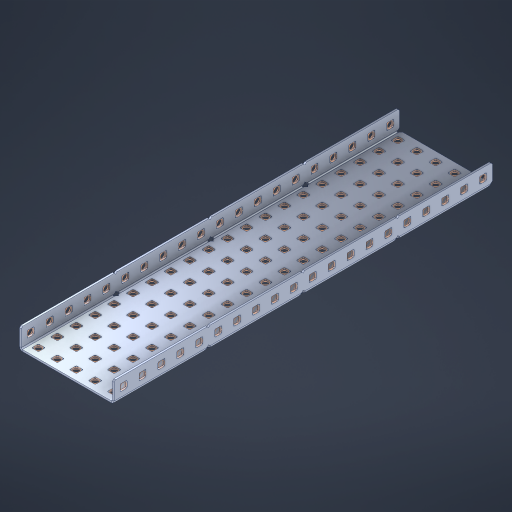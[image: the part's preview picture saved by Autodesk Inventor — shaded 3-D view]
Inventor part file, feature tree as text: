
AUTODESK INVENTOR PART (.ipt)
format: ipt  version: 2023 (Build 270158000, 158)  size: 1,673,728 bytes
history: native  units: in
note: dims shown in document units (in); Inventor stores cm internally (conversion verified against a paired STEP export)
features: other x145, extrude x139, sheet_metal_op x10, sketch x8, mirror x1, pattern_linear x1, chamfer x1
ambient origin geometry x8: Origin, YZ Plane, XZ Plane, XY Plane, X Axis, Y Axis, Z Axis, Center Point
bodies: Solid1 (feature_tree), Body (feature_tree)
feature tree (305):
  other  "Flange Pattern Plane"
  sheet_metal_op  "Flange Pattern"
  sheet_metal_op  "Body Pattern"
  other  "Arc Length"
  mirror  "Notch Mirror"
  pattern_linear  "Notch Pattern"  Spacing1=0.1875in  [1 undecoded]
  chamfer  "End Chamfer"
  extrude  "Half Cut"  Depth=0.0469in
  sketch  "Sketch1"  dims[d0=2.5in]
  other  "Plate1"
  sketch  "Sketch2"  dims[d1=10.0in]
  other  "Plate2"
  sheet_metal_op  "Bend1"
  sheet_metal_op  "Corner1"
  sketch  "Sketch3"  dims[d2=0.0469in]
  other  "Flange Pattern Sketch"
  sketch  "Sketch7"  dims[d3=0.0469in]
  other  "Srf1"
  other  "Srf2"
  sketch  "Sketch8"  dims[d4=0.0234in]
  sketch  "Sketch9"  dims[d5=0.0938in]
  other  "Srf91"
  sheet_metal_op  "Body Pattern Sketch"
  other  "Srf92"
  sketch  "Sketch13"  dims[d6=0.0469in]
  sketch  "Sketch14"  dims[d7=0.5in d8=90.0deg d9=0.0312in d10=0.1875in d11=0.0469in d12=0.0469in d16=0.182in d17=0.02in d18=0.0469in d19=0.0in d20=0.25in d21=0.25in d46=0.172in d47=1.0in d48=0.0in d49=0.182in d50=0.02in d51=0.25in d52=0.25in d53=0.0469in d54=0.0in d55=0.172in d56=1.0in d57=0.0in d60=7.874in d62=0.5in d63=1.9685in d65=0.5in d85=0.1227in d86=0.1659in d88=0.04in d89=0.0469in d90=0.0in d91=0.04in d92=0.0491in d95=2.5in d96=0.04in d97=0.25in d98=45.0deg d101=0.0in d102=2.497in d131=2.5in d132=7.874in d134=0.5in d139=0.5in]
  other  "Srf856"
  other  "Srf1310"
  other  "Srf1311"
  other  "Srf1312"
  other  "Srf1376"
  other  "Srf1377"
  other  "Srf1728"
  other  "Srf1755"
  other  "Srf1878"
  other  "Srf1879"
  other  "Srf1880"
  other  "Srf1881"
  other  "Srf1882"
  other  "Srf1883"
  other  "Srf1884"
  other  "Srf1885"
  other  "Srf1886"
  other  "Srf1887"
  other  "Srf1888"
  other  "Srf1889"
  other  "Srf1890"
  other  "Srf1891"
  other  "Srf1892"
  other  "Srf1893"
  other  "Srf1894"
  other  "Srf1895"
  other  "Srf1896"
  other  "Srf1897"
  other  "Srf1898"
  other  "Srf1899"
  other  "Srf1900"
  other  "Srf1901"
  other  "Srf1902"
  other  "Srf1903"
  other  "Srf1904"
  other  "Srf1905"
  other  "Srf1906"
  other  "Srf1942"
  other  "Srf1943"
  other  "Srf1944"
  other  "Srf1945"
  other  "Srf1946"
  other  "Srf1947"
  other  "Srf1948"
  other  "Srf1949"
  other  "Srf1950"
  other  "Srf1951"
  other  "Srf1952"
  other  "Srf1953"
  other  "Srf1954"
  other  "Srf1955"
  other  "Srf1956"
  other  "Srf1957"
  other  "Srf1958"
  other  "Srf1959"
  other  "Srf1960"
  other  "Srf1961"
  other  "Srf1962"
  other  "Srf1963"
  other  "Srf1964"
  other  "Srf1965"
  other  "Srf1966"
  other  "Srf1967"
  other  "Srf1968"
  other  "Srf1969"
  other  "Srf1970"
  other  "Srf2111"
  other  "Srf2112"
  other  "Srf2113"
  other  "Srf2114"
  other  "Srf2115"
  other  "Srf2146"
  other  "Srf2147"
  other  "Srf2148"
  other  "Srf2149"
  other  "Srf2150"
  other  "Srf2151"
  other  "Srf2152"
  other  "Srf2153"
  other  "Srf2154"
  other  "Srf2155"
  other  "Srf2156"
  other  "Srf2157"
  other  "Srf2158"
  other  "Srf2159"
  other  "Srf2160"
  other  "Srf2161"
  other  "Srf2162"
  other  "Srf2163"
  other  "Srf2164"
  other  "Srf2165"
  other  "Srf2166"
  other  "Srf2167"
  other  "Srf2168"
  other  "Srf2169"
  other  "Srf2170"
  other  "Srf2171"
  other  "Srf2172"
  other  "Srf2173"
  other  "Srf2174"
  other  "Srf2175"
  other  "Srf2176"
  other  "Srf2177"
  other  "Srf2178"
  other  "Srf2179"
  other  "Srf2180"
  other  "Srf2181"
  other  "Srf2182"
  other  "Srf2183"
  other  "Srf2184"
  other  "Srf2185"
  other  "Srf2186"
  other  "Srf2187"
  other  "Srf2188"
  other  "Srf2189"
  other  "Srf2190"
  other  "Srf2191"
  other  "Srf2192"
  other  "Srf2193"
  other  "Srf2194"
  other  "Srf2195"
  other  "Srf2196"
  other  "Srf2197"
  other  "Srf2198"
  other  "Srf2199"
  other  "Srf2200"
  other  "Srf2201"
  other  "Srf2202"
  other  "Srf2203"
  other  "Srf2204"
  other  "Srf2205"
  other  "Srf2206"
  other  "Srf2207"
  other  "Srf2208"
  other  "Srf2209"
  other  "Srf2210"
  sheet_metal_op  "Flange Stamp"
  sheet_metal_op  "Flange Circle"
  sheet_metal_op  "Body Stamp"
  sheet_metal_op  "Body Circle"
  sheet_metal_op  "Notch"
  extrude  "ExtrusionSrf2"  Depth=0.0469in
  extrude  "ExtrusionSrf92"  Depth=2.5in
  extrude  "ExtrusionSrf856"  Depth=0.02in
  extrude  "ExtrusionSrf1310"  Depth=0.0469in
  extrude  "ExtrusionSrf1311"  TaperAngle=0.0deg  [1 undecoded]
  extrude  "ExtrusionSrf1312"  Depth=0.25in
  extrude  "ExtrusionSrf1376"  Depth=0.25in
  extrude  "ExtrusionSrf1377"  Depth=2.5in
  extrude  "ExtrusionSrf1728"  Depth=2.5in TaperAngle=0.0deg
  extrude  "ExtrusionSrf1755"  Depth=2.5in
  extrude  "ExtrusionSrf1878"  Depth=0.02in
  extrude  "ExtrusionSrf1879"  Depth=0.25in
  extrude  "ExtrusionSrf1880"  Depth=0.25in
  extrude  "ExtrusionSrf1881"  Depth=0.0469in
  extrude  "ExtrusionSrf1882"  TaperAngle=0.0deg  [1 undecoded]
  extrude  "ExtrusionSrf1883"  Depth=2.5in
  extrude  "ExtrusionSrf1884"  Depth=2.5in TaperAngle=0.0deg
  extrude  "ExtrusionSrf1885"  Depth=2.5in
  extrude  "ExtrusionSrf1886"  Depth=2.5in
  extrude  "ExtrusionSrf1887"  Depth=2.5in
  extrude  "ExtrusionSrf1888"  Depth=2.5in
  extrude  "ExtrusionSrf1889"  Depth=2.5in
  extrude  "ExtrusionSrf1890"  Depth=0.0469in
  extrude  "ExtrusionSrf1891"  TaperAngle=0.0deg  [1 undecoded]
  extrude  "ExtrusionSrf1892"  Depth=2.5in
  extrude  "ExtrusionSrf1893"  Depth=2.5in
  extrude  "ExtrusionSrf1894"  Depth=2.5in
  extrude  "ExtrusionSrf1895"  Depth=0.25in TaperAngle=45.0deg
  extrude  "ExtrusionSrf1896"  TaperAngle=0.0deg  [1 undecoded]
  extrude  "ExtrusionSrf1897"  Depth=2.5in
  extrude  "ExtrusionSrf1898"  Depth=2.5in
  extrude  "ExtrusionSrf1899"  Depth=2.5in
  extrude  "ExtrusionSrf1900"  Depth=2.5in
  extrude  "ExtrusionSrf1901"  Depth=2.5in
  extrude  "ExtrusionSrf1902"  [1 undecoded]
  extrude  "ExtrusionSrf1903"  [1 undecoded]
  extrude  "ExtrusionSrf1904"  [1 undecoded]
  extrude  "ExtrusionSrf1905"  [1 undecoded]
  extrude  "ExtrusionSrf1906"  [1 undecoded]
  extrude  "ExtrusionSrf1942"  [1 undecoded]
  extrude  "ExtrusionSrf1943"  [1 undecoded]
  extrude  "ExtrusionSrf1944"  [1 undecoded]
  extrude  "ExtrusionSrf1945"  [1 undecoded]
  extrude  "ExtrusionSrf1946"  [1 undecoded]
  extrude  "ExtrusionSrf1947"  [1 undecoded]
  extrude  "ExtrusionSrf1948"  [1 undecoded]
  extrude  "ExtrusionSrf1949"  [1 undecoded]
  extrude  "ExtrusionSrf1950"  [1 undecoded]
  extrude  "ExtrusionSrf1951"  [1 undecoded]
  extrude  "ExtrusionSrf1952"  [1 undecoded]
  extrude  "ExtrusionSrf1953"  [1 undecoded]
  extrude  "ExtrusionSrf1954"  [1 undecoded]
  extrude  "ExtrusionSrf1955"  [1 undecoded]
  extrude  "ExtrusionSrf1956"  [1 undecoded]
  extrude  "ExtrusionSrf1957"  [1 undecoded]
  extrude  "ExtrusionSrf1958"  [1 undecoded]
  extrude  "ExtrusionSrf1959"  [1 undecoded]
  extrude  "ExtrusionSrf1960"  [1 undecoded]
  extrude  "ExtrusionSrf1961"  [1 undecoded]
  extrude  "ExtrusionSrf1962"  [1 undecoded]
  extrude  "ExtrusionSrf1963"  [1 undecoded]
  extrude  "ExtrusionSrf1964"  [1 undecoded]
  extrude  "ExtrusionSrf1965"  [1 undecoded]
  extrude  "ExtrusionSrf1966"  [1 undecoded]
  extrude  "ExtrusionSrf1967"  [1 undecoded]
  extrude  "ExtrusionSrf1968"  [1 undecoded]
  extrude  "ExtrusionSrf1969"  [1 undecoded]
  extrude  "ExtrusionSrf1970"  [1 undecoded]
  extrude  "ExtrusionSrf2111"  [1 undecoded]
  extrude  "ExtrusionSrf2112"  [1 undecoded]
  extrude  "ExtrusionSrf2113"  [1 undecoded]
  extrude  "ExtrusionSrf2114"  [1 undecoded]
  extrude  "ExtrusionSrf2115"  [1 undecoded]
  extrude  "ExtrusionSrf2146"  [1 undecoded]
  extrude  "ExtrusionSrf2147"  [1 undecoded]
  extrude  "ExtrusionSrf2148"  [1 undecoded]
  extrude  "ExtrusionSrf2149"  [1 undecoded]
  extrude  "ExtrusionSrf2150"  [1 undecoded]
  extrude  "ExtrusionSrf2151"  [1 undecoded]
  extrude  "ExtrusionSrf2152"  [1 undecoded]
  extrude  "ExtrusionSrf2153"  [1 undecoded]
  extrude  "ExtrusionSrf2154"  [1 undecoded]
  extrude  "ExtrusionSrf2155"  [1 undecoded]
  extrude  "ExtrusionSrf2156"  [1 undecoded]
  extrude  "ExtrusionSrf2157"  [1 undecoded]
  extrude  "ExtrusionSrf2158"  [1 undecoded]
  extrude  "ExtrusionSrf2159"  [1 undecoded]
  extrude  "ExtrusionSrf2160"  [1 undecoded]
  extrude  "ExtrusionSrf2161"  [1 undecoded]
  extrude  "ExtrusionSrf2162"  [1 undecoded]
  extrude  "ExtrusionSrf2163"  [1 undecoded]
  extrude  "ExtrusionSrf2164"  [1 undecoded]
  extrude  "ExtrusionSrf2165"  [1 undecoded]
  extrude  "ExtrusionSrf2166"  [1 undecoded]
  extrude  "ExtrusionSrf2167"  [1 undecoded]
  extrude  "ExtrusionSrf2168"  [1 undecoded]
  extrude  "ExtrusionSrf2169"  [1 undecoded]
  extrude  "ExtrusionSrf2170"  [1 undecoded]
  extrude  "ExtrusionSrf2171"  [1 undecoded]
  extrude  "ExtrusionSrf2172"  [1 undecoded]
  extrude  "ExtrusionSrf2173"  [1 undecoded]
  extrude  "ExtrusionSrf2174"  [1 undecoded]
  extrude  "ExtrusionSrf2175"  [1 undecoded]
  extrude  "ExtrusionSrf2176"  [1 undecoded]
  extrude  "ExtrusionSrf2177"  [1 undecoded]
  extrude  "ExtrusionSrf2178"  [1 undecoded]
  extrude  "ExtrusionSrf2179"  [1 undecoded]
  extrude  "ExtrusionSrf2180"  [1 undecoded]
  extrude  "ExtrusionSrf2181"  [1 undecoded]
  extrude  "ExtrusionSrf2182"  [1 undecoded]
  extrude  "ExtrusionSrf2183"  [1 undecoded]
  extrude  "ExtrusionSrf2184"  [1 undecoded]
  extrude  "ExtrusionSrf2185"  [1 undecoded]
  extrude  "ExtrusionSrf2186"  [1 undecoded]
  extrude  "ExtrusionSrf2187"  [1 undecoded]
  extrude  "ExtrusionSrf2188"  [1 undecoded]
  extrude  "ExtrusionSrf2189"  [1 undecoded]
  extrude  "ExtrusionSrf2190"  [1 undecoded]
  extrude  "ExtrusionSrf2191"  [1 undecoded]
  extrude  "ExtrusionSrf2192"  [1 undecoded]
  extrude  "ExtrusionSrf2193"  [1 undecoded]
  extrude  "ExtrusionSrf2194"  [1 undecoded]
  extrude  "ExtrusionSrf2195"  [1 undecoded]
  extrude  "ExtrusionSrf2196"  [1 undecoded]
  extrude  "ExtrusionSrf2197"  [1 undecoded]
  extrude  "ExtrusionSrf2198"  [1 undecoded]
  extrude  "ExtrusionSrf2199"  [1 undecoded]
  extrude  "ExtrusionSrf2200"  [1 undecoded]
  extrude  "ExtrusionSrf2201"  [1 undecoded]
  extrude  "ExtrusionSrf2202"  [1 undecoded]
  extrude  "ExtrusionSrf2203"  [1 undecoded]
  extrude  "ExtrusionSrf2204"  [1 undecoded]
  extrude  "ExtrusionSrf2205"  [1 undecoded]
  extrude  "ExtrusionSrf2206"  [1 undecoded]
  extrude  "ExtrusionSrf2207"  [1 undecoded]
  extrude  "ExtrusionSrf2208"  [1 undecoded]
  extrude  "ExtrusionSrf2209"  [1 undecoded]
  extrude  "ExtrusionSrf2210"  [1 undecoded]
note: 109 required parameter values undecoded (feature->parameter linkage not recoverable at this tier; creation-order binding heuristic only, values carry confidence <= 0.55)
